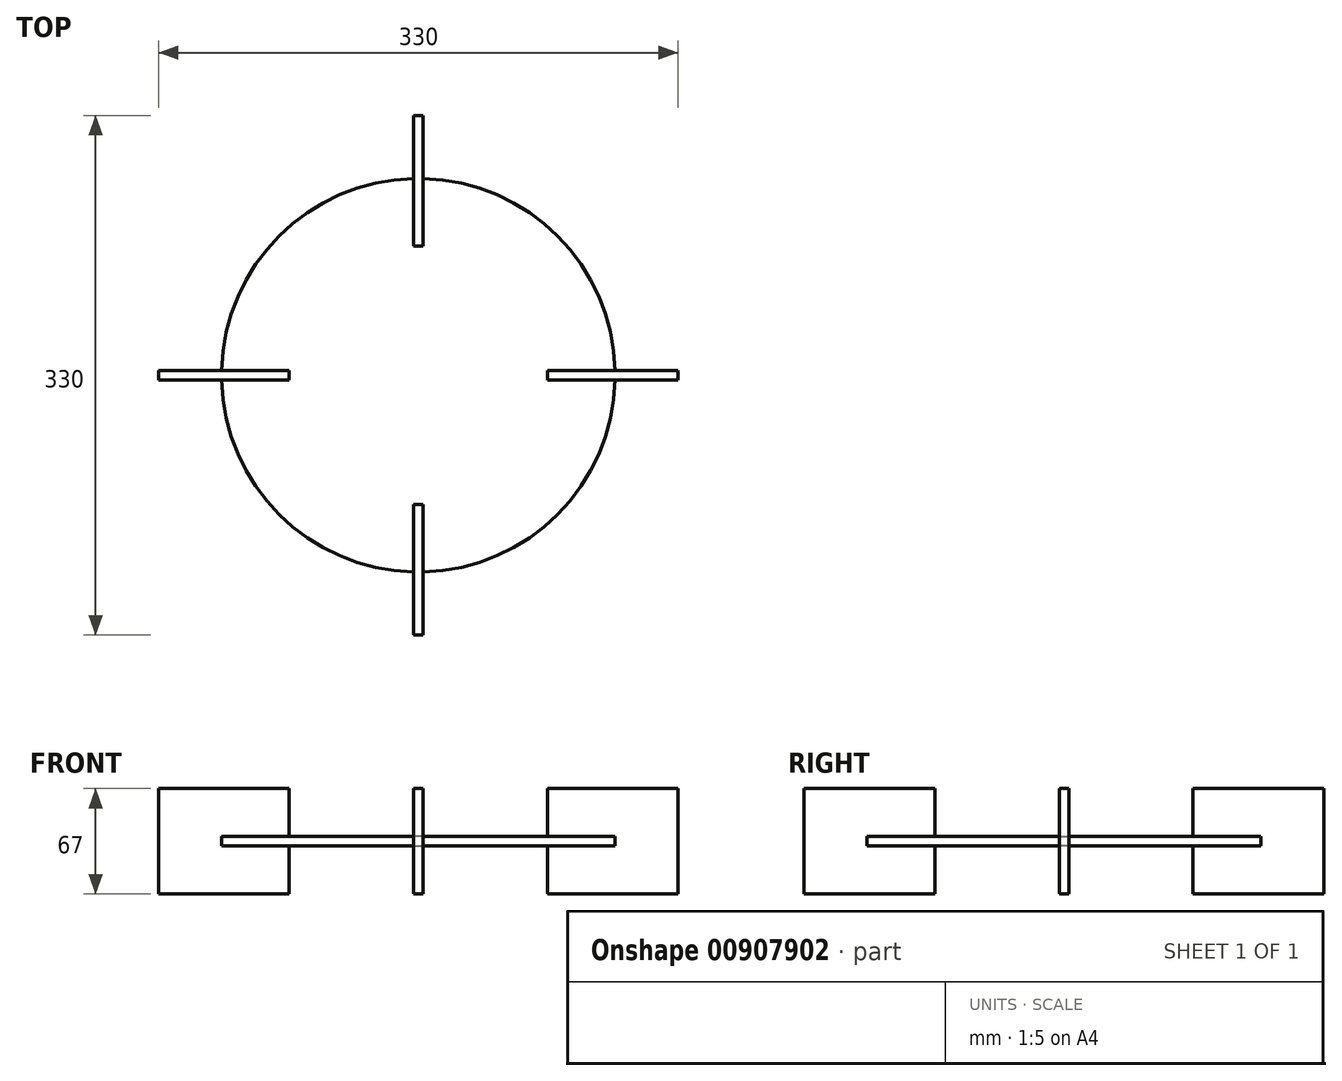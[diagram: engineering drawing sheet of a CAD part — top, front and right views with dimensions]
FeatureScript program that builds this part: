
annotation { "Feature Type Name" : "Feature", "Feature Type Description" : "" }
export const myFeature = defineFeature(function(context is Context, id is Id, definition is map)
    precondition{}
    {
        {
            var Q0;
            Q0=qCreatedBy(makeId("Top.planeOp"),FACE);
            var sketch = newSketch(context, id + "F0", { "sketchPlane" : qUnion([Q0])});
            skCircle(sketch, "E0", {"center": v(0, 0) * mm, "radius": 125 * mm});
            skLineSegment(sketch, "E1", {"start": v(0, 0) * mm, "end": v(50, 0) * mm, "construction": true});
            skCircle(sketch, "E2", {"center": v(50, 0) * mm, "radius": 4.76 * mm, "construction": true});
            skCircle(sketch, "E3.1.0", {"center": v(0, 50) * mm, "radius": 4.76 * mm, "construction": true});
            skCircle(sketch, "E3.2.0", {"center": v(-50, 0) * mm, "radius": 4.76 * mm, "construction": true});
            skCircle(sketch, "E3.3.0", {"center": v(0, -50) * mm, "radius": 4.76 * mm, "construction": true});
            skSolve(sketch);
        }
        {
            var Q0;
            Q0 = qSketchRegion(id + "F0", true);
            extrude(context, id + "F1", {"entities" : qUnion([Q0]), "depth" : 6 * mm, "offsetDistance" : 25 * mm});
        }
        {
            var Q0;
            Q0=makeQuery(id+"F1.opExtrude","CAP_FACE",FACE,{"disambiguationData":[OSD([sQuery(id+"F0.wireOp",EDGE,"E0")])],"isStart":false});
            var Q1;
            Q1=makeQuery(id+"F1.opExtrude","CAP_FACE",FACE,{"disambiguationData":[OSD([sQuery(id+"F0.wireOp",EDGE,"E0")])],"isStart":true});
            cPlane(context, id + "F2", {"entities" : qUnion([Q0, Q1]), "cplaneType" : CPlaneType.MID_PLANE, "offset" : 25 * mm, "width" : 150 * mm, "height" : 150 * mm});
        }
        {
            var Q0;
            Q0=qCreatedBy(id+"F2.planeOp",FACE);
            var sketch = newSketch(context, id + "F3", { "sketchPlane" : qUnion([Q0])});
            skLineSegment(sketch, "E4.3.0", {"start": v(3, 82) * mm, "end": v(3, 165) * mm});
            skLineSegment(sketch, "E4.3.1", {"start": v(-3, 82) * mm, "end": v(-3, 165) * mm});
            skLineSegment(sketch, "E4.3.2", {"start": v(3, 165) * mm, "end": v(-3, 165) * mm});
            skLineSegment(sketch, "E5", {"start": v(-3, 82) * mm, "end": v(3, 82) * mm});
            skLineSegment(sketch, "E6", {"start": v(0, 0) * mm, "end": v(0, 82) * mm, "construction": true});
            skLineSegment(sketch, "E7.1.0", {"start": v(-165, 3) * mm, "end": v(-165, -3) * mm});
            skLineSegment(sketch, "E7.1.1", {"start": v(-82, 3) * mm, "end": v(-165, 3) * mm});
            skLineSegment(sketch, "E7.1.2", {"start": v(-82, -3) * mm, "end": v(-165, -3) * mm});
            skLineSegment(sketch, "E7.1.3", {"start": v(-82, -3) * mm, "end": v(-82, 3) * mm});
            skLineSegment(sketch, "E7.2.0", {"start": v(-3, -165) * mm, "end": v(3, -165) * mm});
            skLineSegment(sketch, "E7.2.1", {"start": v(-3, -82) * mm, "end": v(-3, -165) * mm});
            skLineSegment(sketch, "E7.2.2", {"start": v(3, -82) * mm, "end": v(3, -165) * mm});
            skLineSegment(sketch, "E7.2.3", {"start": v(3, -82) * mm, "end": v(-3, -82) * mm});
            skLineSegment(sketch, "E7.3.0", {"start": v(165, -3) * mm, "end": v(165, 3) * mm});
            skLineSegment(sketch, "E7.3.1", {"start": v(82, -3) * mm, "end": v(165, -3) * mm});
            skLineSegment(sketch, "E7.3.2", {"start": v(82, 3) * mm, "end": v(165, 3) * mm});
            skLineSegment(sketch, "E7.3.3", {"start": v(82, 3) * mm, "end": v(82, -3) * mm});
            skPoint(sketch, "E7.center", {"position": v(0, 0) * mm});
            skSolve(sketch);
        }
        {
            var Q0;
            Q0=makeQuery(id+"F3.imprint","IMPRINT",FACE,{"disambiguationData":[TD([[makeQuery(id+"F3.imprint","IMPRINT",EDGE,{"derivedFrom":sQuery(id+"F3.wireOp",EDGE,"E7.1.0")}),1.0]])]});
            var Q1;
            Q1=makeQuery(id+"F3.imprint","IMPRINT",FACE,{"disambiguationData":[TD([[makeQuery(id+"F3.imprint","IMPRINT",EDGE,{"derivedFrom":sQuery(id+"F3.wireOp",EDGE,"E4.3.0")}),1.0]])]});
            var Q2;
            Q2=makeQuery(id+"F3.imprint","IMPRINT",FACE,{"disambiguationData":[TD([[makeQuery(id+"F3.imprint","IMPRINT",EDGE,{"derivedFrom":sQuery(id+"F3.wireOp",EDGE,"E7.3.0")}),1.0]])]});
            var Q3;
            Q3=makeQuery(id+"F3.imprint","IMPRINT",FACE,{"disambiguationData":[TD([[makeQuery(id+"F3.imprint","IMPRINT",EDGE,{"derivedFrom":sQuery(id+"F3.wireOp",EDGE,"E7.2.0")}),1.0]])]});
            extrude(context, id + "F4", {"entities" : qUnion([Q0, Q1, Q2, Q3]), "operationType" : NewBodyOperationType.ADD, "depth" : 67 * mm / 2, "offsetDistance" : 25 * mm, "hasSecondDirection" : true, "secondDirectionOppositeDirection" : true, "secondDirectionDepth" : 33.5 * mm});
        }
    });
